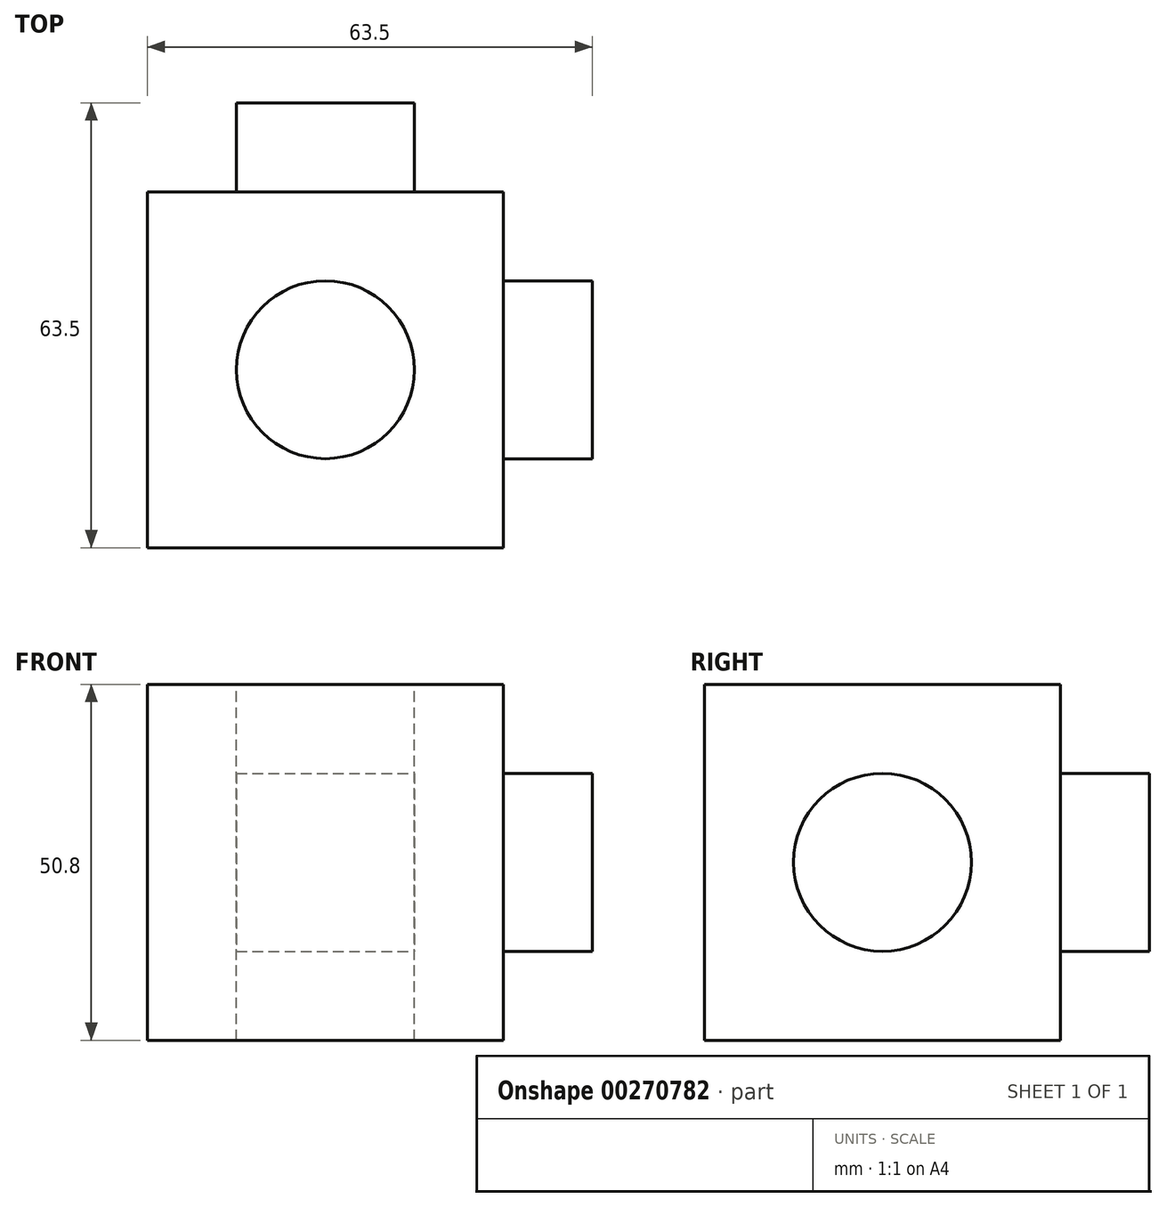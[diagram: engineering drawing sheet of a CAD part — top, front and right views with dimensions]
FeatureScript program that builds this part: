
annotation { "Feature Type Name" : "Feature", "Feature Type Description" : "" }
export const myFeature = defineFeature(function(context is Context, id is Id, definition is map)
    precondition{}
    {
        {
            var Q0;
            Q0=qCreatedBy(makeId("Front.planeOp"),FACE);
            var sketch = newSketch(context, id + "F0", { "sketchPlane" : qUnion([Q0])});
            skLineSegment(sketch, "E0.bottom", {"start": v(0, 0) * mm, "end": v(-50.8, 0) * mm});
            skLineSegment(sketch, "E0.top", {"start": v(0, 50.8) * mm, "end": v(-50.8, 50.8) * mm});
            skLineSegment(sketch, "E0.left", {"start": v(0, 0) * mm, "end": v(0, 50.8) * mm});
            skLineSegment(sketch, "E0.right", {"start": v(-50.8, 0) * mm, "end": v(-50.8, 50.8) * mm});
            skSolve(sketch);
        }
        {
            var Q0;
            Q0 = qSketchRegion(id + "F0", true);
            extrude(context, id + "F1", {"entities" : qUnion([Q0]), "depth" : 50.8 * mm});
        }
        {
            var Q0;
            Q0=makeQuery(id+"F1.opExtrude","SWEPT_FACE",FACE,{"disambiguationData":[OSD([sQuery(id+"F0.wireOp",EDGE,"E0.top")])]});
            var sketch = newSketch(context, id + "F2", { "sketchPlane" : qUnion([Q0])});
            skCircle(sketch, "E1", {"center": v(-25.4, -25.4) * mm, "radius": 12.7 * mm});
            skSolve(sketch);
        }
        {
            var Q0;
            Q0 = qSketchRegion(id + "F2", true);
            extrude(context, id + "F3", {"entities" : qUnion([Q0]), "operationType" : NewBodyOperationType.REMOVE, "oppositeDirection" : true, "depth" : 50.8 * mm});
        }
        {
            var Q0;
            Q0=makeQuery(id+"F1.opExtrude","SWEPT_FACE",FACE,{"disambiguationData":[OSD([sQuery(id+"F0.wireOp",EDGE,"E0.left")])]});
            var sketch = newSketch(context, id + "F4", { "sketchPlane" : qUnion([Q0])});
            skCircle(sketch, "E2", {"center": v(-25.4, 25.4) * mm, "radius": 12.7 * mm});
            skSolve(sketch);
        }
        {
            var Q0;
            Q0 = qSketchRegion(id + "F4", true);
            extrude(context, id + "F5", {"entities" : qUnion([Q0]), "operationType" : NewBodyOperationType.ADD, "depth" : 12.7 * mm});
        }
        {
            var Q0;
            Q0=qCreatedBy(makeId("Front.planeOp"),FACE);
            var sketch = newSketch(context, id + "F6", { "sketchPlane" : qUnion([Q0])});
            skLineSegment(sketch, "E3.bottom", {"start": v(-38.1, 38.1) * mm, "end": v(-12.7, 38.1) * mm});
            skLineSegment(sketch, "E3.top", {"start": v(-38.1, 12.7) * mm, "end": v(-12.7, 12.7) * mm});
            skLineSegment(sketch, "E3.left", {"start": v(-38.1, 38.1) * mm, "end": v(-38.1, 12.7) * mm});
            skLineSegment(sketch, "E3.right", {"start": v(-12.7, 38.1) * mm, "end": v(-12.7, 12.7) * mm});
            skSolve(sketch);
        }
        {
            var Q0;
            Q0 = qSketchRegion(id + "F6", true);
            extrude(context, id + "F7", {"entities" : qUnion([Q0]), "operationType" : NewBodyOperationType.ADD, "oppositeDirection" : true, "depth" : 12.7 * mm});
        }
    });
